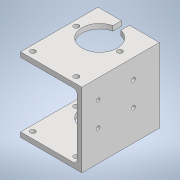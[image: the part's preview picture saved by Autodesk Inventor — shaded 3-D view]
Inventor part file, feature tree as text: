
AUTODESK INVENTOR PART (.ipt)
format: ipt  version: 2022 (Build 260153000, 153)  size: 194,560 bytes
history: native  units: mm
features: sketch x7, extrude x3, hole x3, other x1, fillet x1
ambient origin geometry x8: Origin, YZ Plane, XZ Plane, XY Plane, X Axis, Y Axis, Z Axis, Center Point
bodies: Body1 (feature_tree)
feature tree (15):
  other  "ソリッド1"
  extrude  "押し出し1"  Depth=48.0mm
  extrude  "押し出し2"  Depth=38.0mm
  hole  "穴1"  [1 undecoded]
  hole  "穴2"  [1 undecoded]
  sketch  "スケッチ6"
  fillet  "フィレット1"  Radius=3.0mm
  hole  "穴5"  [1 undecoded]
  extrude  "押し出し4"  Depth=100.0mm TaperAngle=0.0deg
  sketch  "スケッチ1"
  sketch  "スケッチ2"
  sketch  "スケッチ3"
  sketch  "スケッチ4"
  sketch  "スケッチ8"
  sketch  "スケッチ9"
note: 3 required parameter values undecoded (feature->parameter linkage not recoverable at this tier; creation-order binding heuristic only, values carry confidence <= 0.55)
